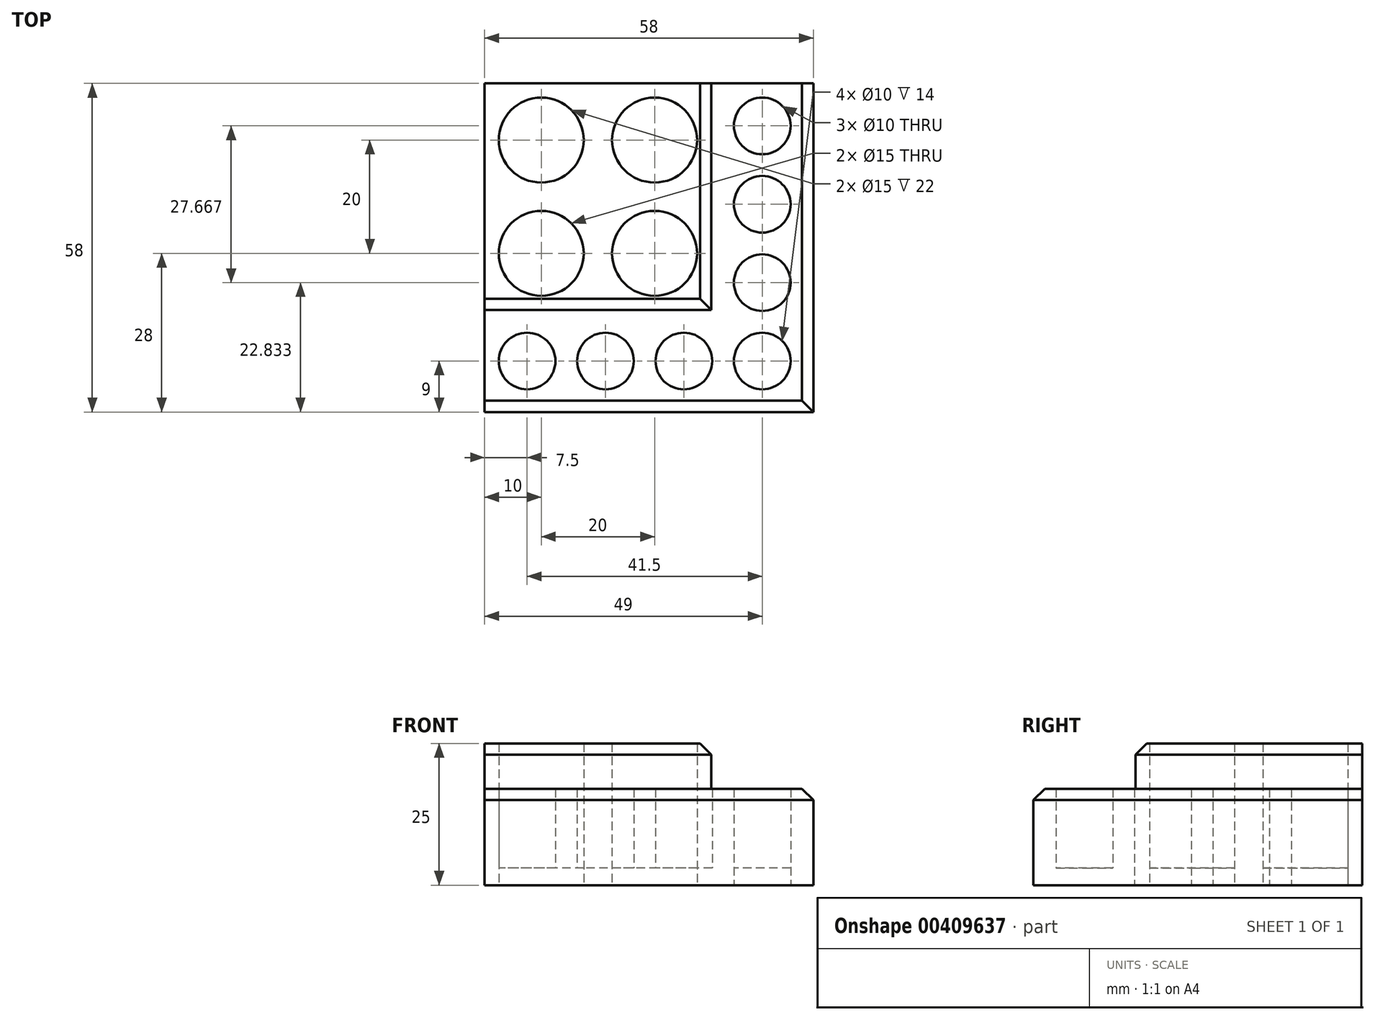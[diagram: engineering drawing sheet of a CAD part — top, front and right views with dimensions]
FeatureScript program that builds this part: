
annotation { "Feature Type Name" : "Feature", "Feature Type Description" : "" }
export const myFeature = defineFeature(function(context is Context, id is Id, definition is map)
    precondition{}
    {
        {
            var Q0;
            Q0=qCreatedBy(makeId("Top.planeOp"),FACE);
            var sketch = newSketch(context, id + "F0", { "sketchPlane" : qUnion([Q0])});
            skLineSegment(sketch, "E0.bottom", {"start": v(0, 0) * mm, "end": v(40, 0) * mm});
            skLineSegment(sketch, "E0.top", {"start": v(0, -40) * mm, "end": v(40, -40) * mm});
            skLineSegment(sketch, "E0.left", {"start": v(0, 0) * mm, "end": v(0, -40) * mm});
            skLineSegment(sketch, "E0.right", {"start": v(40, 0) * mm, "end": v(40, -40) * mm});
            skLineSegment(sketch, "E1", {"start": v(0, -40) * mm, "end": v(0, -58) * mm});
            skLineSegment(sketch, "E2", {"start": v(40, 0) * mm, "end": v(58, 0) * mm});
            skLineSegment(sketch, "E3", {"start": v(0, -58) * mm, "end": v(58, -58) * mm});
            skLineSegment(sketch, "E4", {"start": v(58, -58) * mm, "end": v(58, 0) * mm});
            skLineSegment(sketch, "E5", {"start": v(0, -20) * mm, "end": v(40, -20) * mm, "construction": true});
            skLineSegment(sketch, "E6", {"start": v(20, 0) * mm, "end": v(20, -40) * mm, "construction": true});
            skLineSegment(sketch, "E7", {"start": v(20, 0) * mm, "end": v(0, 0) * mm});
            skLineSegment(sketch, "E8", {"start": v(0, -20) * mm, "end": v(0, 0) * mm});
            skCircle(sketch, "E9", {"center": v(10, -10) * mm, "radius": 7.5 * mm});
            skPoint(sketch, "E9.centerSnap0", {"position": v(0, -10) * mm});
            skPoint(sketch, "E9.centerSnap1", {"position": v(10, 0) * mm});
            skCircle(sketch, "E10.MirrorC", {"center": v(30, -10) * mm, "radius": 7.5 * mm});
            skCircle(sketch, "E11.MirrorC", {"center": v(10, -30) * mm, "radius": 7.5 * mm});
            skCircle(sketch, "E12.MirrorC", {"center": v(30, -30) * mm, "radius": 7.5 * mm});
            skCircle(sketch, "E13", {"center": v(7.5, -49) * mm, "radius": 5 * mm});
            skPoint(sketch, "E13.centerSnap0", {"position": v(0, -49) * mm});
            skLineSegment(sketch, "E14", {"start": v(40, -40) * mm, "end": v(58, -58) * mm, "construction": true});
            skCircle(sketch, "E15.1.0.0", {"center": v(21.33, -49) * mm, "radius": 5 * mm});
            skCircle(sketch, "E15.2.0.0", {"center": v(35.17, -49) * mm, "radius": 5 * mm});
            skCircle(sketch, "E15.3.0.0", {"center": v(49, -49) * mm, "radius": 5 * mm});
            skLineSegment(sketch, "E15.direction1", {"start": v(7.5, -49) * mm, "end": v(21.33, -49) * mm, "construction": true});
            skCircle(sketch, "E16.MirrorC", {"center": v(49, -7.5) * mm, "radius": 5 * mm});
            skCircle(sketch, "E17.MirrorC", {"center": v(49, -21.33) * mm, "radius": 5 * mm});
            skCircle(sketch, "E18.MirrorC", {"center": v(49, -35.17) * mm, "radius": 5 * mm});
            skSolve(sketch);
        }
        {
            var Q0;
            Q0=makeQuery(id+"F0.imprint","IMPRINT",FACE,{"disambiguationData":[TD([[makeQuery(id+"F0.imprint","IMPRINT",EDGE,{"derivedFrom":sQuery(id+"F0.wireOp",EDGE,"E0.bottom")}),-1.0]])]});
            extrude(context, id + "F1", {"entities" : qUnion([Q0]), "depth" : 25 * mm});
        }
        {
            var Q0;
            Q0=makeQuery(id+"F0.imprint","IMPRINT",FACE,{"disambiguationData":[TD([[makeQuery(id+"F0.imprint","IMPRINT",EDGE,{"derivedFrom":sQuery(id+"F0.wireOp",EDGE,"E0.top")}),-1.0]])]});
            extrude(context, id + "F2", {"entities" : qUnion([Q0]), "operationType" : NewBodyOperationType.ADD, "depth" : 17 * mm});
        }
        {
            var Q0;
            Q0=makeQuery(id+"F0.imprint","IMPRINT",FACE,{"disambiguationData":[TD([[makeQuery(id+"F0.imprint","IMPRINT",EDGE,{"derivedFrom":sQuery(id+"F0.wireOp",EDGE,"E9")}),1.0]])]});
            var Q1;
            Q1=makeQuery(id+"F0.imprint","IMPRINT",FACE,{"disambiguationData":[TD([[makeQuery(id+"F0.imprint","IMPRINT",EDGE,{"derivedFrom":sQuery(id+"F0.wireOp",EDGE,"E10.MirrorC")}),-1.0]])]});
            var Q2;
            Q2=makeQuery(id+"F0.imprint","IMPRINT",FACE,{"disambiguationData":[TD([[makeQuery(id+"F0.imprint","IMPRINT",EDGE,{"derivedFrom":sQuery(id+"F0.wireOp",EDGE,"E12.MirrorC")}),1.0]])]});
            var Q3;
            Q3=makeQuery(id+"F0.imprint","IMPRINT",FACE,{"disambiguationData":[TD([[makeQuery(id+"F0.imprint","IMPRINT",EDGE,{"derivedFrom":sQuery(id+"F0.wireOp",EDGE,"E11.MirrorC")}),-1.0]])]});
            var Q4;
            Q4=makeQuery(id+"F0.imprint","IMPRINT",FACE,{"disambiguationData":[TD([[makeQuery(id+"F0.imprint","IMPRINT",EDGE,{"derivedFrom":sQuery(id+"F0.wireOp",EDGE,"E13")}),1.0]])]});
            var Q5;
            Q5=makeQuery(id+"F0.imprint","IMPRINT",FACE,{"disambiguationData":[TD([[makeQuery(id+"F0.imprint","IMPRINT",EDGE,{"derivedFrom":sQuery(id+"F0.wireOp",EDGE,"E15.1.0.0")}),1.0]])]});
            var Q6;
            Q6=makeQuery(id+"F0.imprint","IMPRINT",FACE,{"disambiguationData":[TD([[makeQuery(id+"F0.imprint","IMPRINT",EDGE,{"derivedFrom":sQuery(id+"F0.wireOp",EDGE,"E15.2.0.0")}),1.0]])]});
            var Q7;
            Q7=makeQuery(id+"F0.imprint","IMPRINT",FACE,{"disambiguationData":[TD([[makeQuery(id+"F0.imprint","IMPRINT",EDGE,{"derivedFrom":sQuery(id+"F0.wireOp",EDGE,"E15.3.0.0")}),1.0]])]});
            var Q8;
            Q8=makeQuery(id+"F0.imprint","IMPRINT",FACE,{"disambiguationData":[TD([[makeQuery(id+"F0.imprint","IMPRINT",EDGE,{"derivedFrom":sQuery(id+"F0.wireOp",EDGE,"E18.MirrorC")}),-1.0]])]});
            var Q9;
            Q9=makeQuery(id+"F0.imprint","IMPRINT",FACE,{"disambiguationData":[TD([[makeQuery(id+"F0.imprint","IMPRINT",EDGE,{"derivedFrom":sQuery(id+"F0.wireOp",EDGE,"E17.MirrorC")}),-1.0]])]});
            var Q10;
            Q10=makeQuery(id+"F0.imprint","IMPRINT",FACE,{"disambiguationData":[TD([[makeQuery(id+"F0.imprint","IMPRINT",EDGE,{"derivedFrom":sQuery(id+"F0.wireOp",EDGE,"E16.MirrorC")}),-1.0]])]});
            extrude(context, id + "F3", {"entities" : qUnion([Q0, Q1, Q2, Q3, Q4, Q5, Q6, Q7, Q8, Q9, Q10]), "operationType" : NewBodyOperationType.ADD, "depth" : 3 * mm});
        }
        {
            var Q0;
            Q0=makeQuery(id+"F1.opExtrude","CAP_EDGE",EDGE,{"disambiguationData":[OSD([sQuery(id+"F0.wireOp",EDGE,"E0.top")])],"isStart":false});
            var Q1;
            Q1=makeQuery(id+"F1.opExtrude","CAP_EDGE",EDGE,{"disambiguationData":[OSD([sQuery(id+"F0.wireOp",EDGE,"E0.right")])],"isStart":false});
            var Q2;
            Q2=makeQuery(id+"F2.opExtrude","CAP_EDGE",EDGE,{"disambiguationData":[OSD([sQuery(id+"F0.wireOp",EDGE,"E3")])],"isStart":false});
            var Q3;
            Q3=makeQuery(id+"F2.opExtrude","CAP_EDGE",EDGE,{"disambiguationData":[OSD([sQuery(id+"F0.wireOp",EDGE,"E4")])],"isStart":false});
            chamfer(context, id + "F4", {"entities" : qUnion([Q0, Q1, Q2, Q3]), "width" : 2 * mm, "tangentPropagation" : true});
        }
    });
